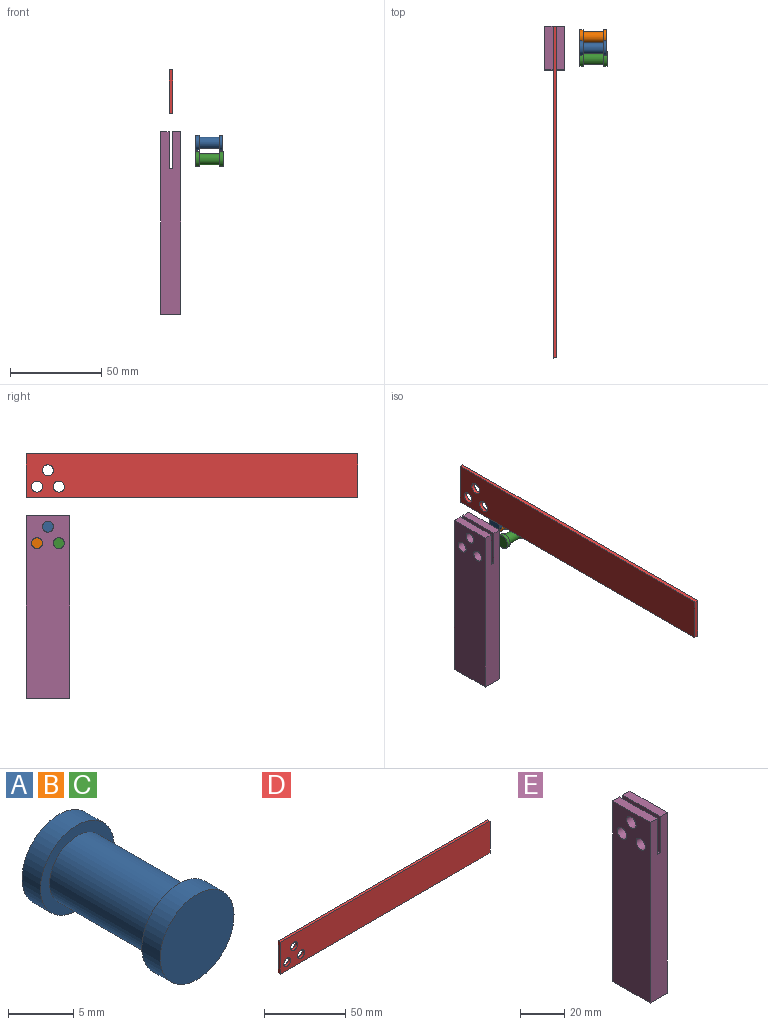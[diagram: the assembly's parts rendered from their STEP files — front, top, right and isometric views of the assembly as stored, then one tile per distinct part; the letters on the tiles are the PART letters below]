
ASSEMBLY  parts=5 mates=4
PART A: 7 faces, bbox 8x15x8 mm
  f0: cylinder r=3mm len=11mm, axis (0,1,0), area 207.3mm2, adj f3,f6
  f1: cylinder r=4mm len=8mm, axis (0,1,0), area 50.3mm2, adj f2,f3
  f2: plane 8x8mm, normal (0,-1,0), area 50.3mm2, adj f1
  f3: plane 8x8mm, normal (0,1,0), area 22mm2, adj f0,f1
  f4: cylinder r=4mm len=8mm, axis (0,-1,0), area 50.3mm2, adj f5,f6
  f5: plane 8x8mm, normal (0,1,0), area 50.3mm2, adj f4
  f6: plane 8x8mm, normal (0,-1,0), area 22mm2, adj f0,f4
PART B: same geometry as A
PART C: same geometry as A
PART D: 9 faces, bbox 182x2x24 mm
  f0: plane 24x2mm, normal (1,0,0), area 48mm2, adj f1,f3,f4,f5
  f1: plane 182x2mm, normal (0,0,1), area 364mm2, adj f0,f2,f4,f5
  f2: plane 24x2mm, normal (-1,0,0), area 48mm2, adj f1,f3,f4,f5
  f3: plane 182x2mm, normal (0,0,-1), area 364mm2, adj f0,f2,f4,f5
  f4: plane 182x24mm, normal (0,-1,0), area 4283.2mm2, adj f0,f1,f2,f3,f6,f7,f8
  f5: plane 182x24mm, normal (0,1,0), area 4283.2mm2, adj f0,f1,f2,f3,f6,f7,f8
  f6: cylinder r=3mm len=6mm, axis (0,-1,0), area 37.7mm2, adj f4,f5
  f7: cylinder r=3mm len=6mm, axis (0,-1,0), area 37.7mm2, adj f4,f5
  f8: cylinder r=3mm len=6mm, axis (0,-1,0), area 37.7mm2, adj f4,f5
PART E: 16 faces, bbox 11x24x100 mm
  f0: plane 24x4.5mm, normal (0,0,1), area 108mm2, adj f2,f5,f6,f7
  f1: plane 24x4.5mm, normal (0,0,1), area 108mm2, adj f2,f3,f6,f8
  f2: plane 100x11mm, normal (0,-1,0), area 1060mm2, adj f0,f1,f3,f4,f5,f7,f8,f9
  f3: plane 100x24mm, normal (-1,0,0), area 2315.2mm2, adj f1,f2,f4,f6,f10,f11,f12
  f4: plane 24x11mm, normal (0,0,-1), area 264mm2, adj f2,f3,f5,f6
  f5: plane 100x24mm, normal (1,0,0), area 2315.2mm2, adj f0,f2,f4,f6,f13,f14,f15
  f6: plane 100x11mm, normal (0,1,0), area 1060mm2, adj f0,f1,f3,f4,f5,f7,f8,f9
  f7: plane 24x20mm, normal (-1,0,0), area 395.2mm2, adj f0,f2,f6,f9,f13,f14,f15
  f8: plane 24x20mm, normal (1,0,0), area 395.2mm2, adj f1,f2,f6,f9,f10,f11,f12
  f9: plane 24x2mm, normal (0,0,1), area 48mm2, adj f2,f6,f7,f8
  f10: cylinder r=3mm len=6mm, axis (-1,0,0), area 84.8mm2, adj f3,f8
  f11: cylinder r=3mm len=6mm, axis (-1,0,0), area 84.8mm2, adj f3,f8
  f12: cylinder r=3mm len=6mm, axis (-1,0,0), area 84.8mm2, adj f3,f8
  f13: cylinder r=3mm len=6mm, axis (-1,0,0), area 84.8mm2, adj f5,f7
  f14: cylinder r=3mm len=6mm, axis (-1,0,0), area 84.8mm2, adj f5,f7
  f15: cylinder r=3mm len=6mm, axis (-1,0,0), area 84.8mm2, adj f5,f7
PLACE A rot(axis=(0.58,0.58,-0.58),120deg) t=(91.01,-18.9,61.65)mm
PLACE B rot(axis=(0.58,0.58,-0.58),120deg) t=(91.01,-12.9,52.65)mm
PLACE C rot(axis=(-0.58,-0.58,-0.58),120deg) t=(91.19,-24.9,52.65)mm
PLACE D rot(axis=(0,0,-1),90deg) t=(65.51,-97.9,89.65)mm
PLACE E t=(64.51,-6.9,17.65)mm fixed
MATE slider B.f1 <-> E.f10  axis (1,0,0) through (80.01,-12.9,52.65)mm
MATE slider A.f1 <-> E.f11  axis (1,0,0) through (80.01,-18.9,61.65)mm
MATE slider D.f3 <-> E.f9  axis (0,0,-1) through (65.51,-6.9,77.65)mm
MATE slider C.f1 <-> E.f12  axis (1,0,0) through (80.19,-24.9,52.65)mm
